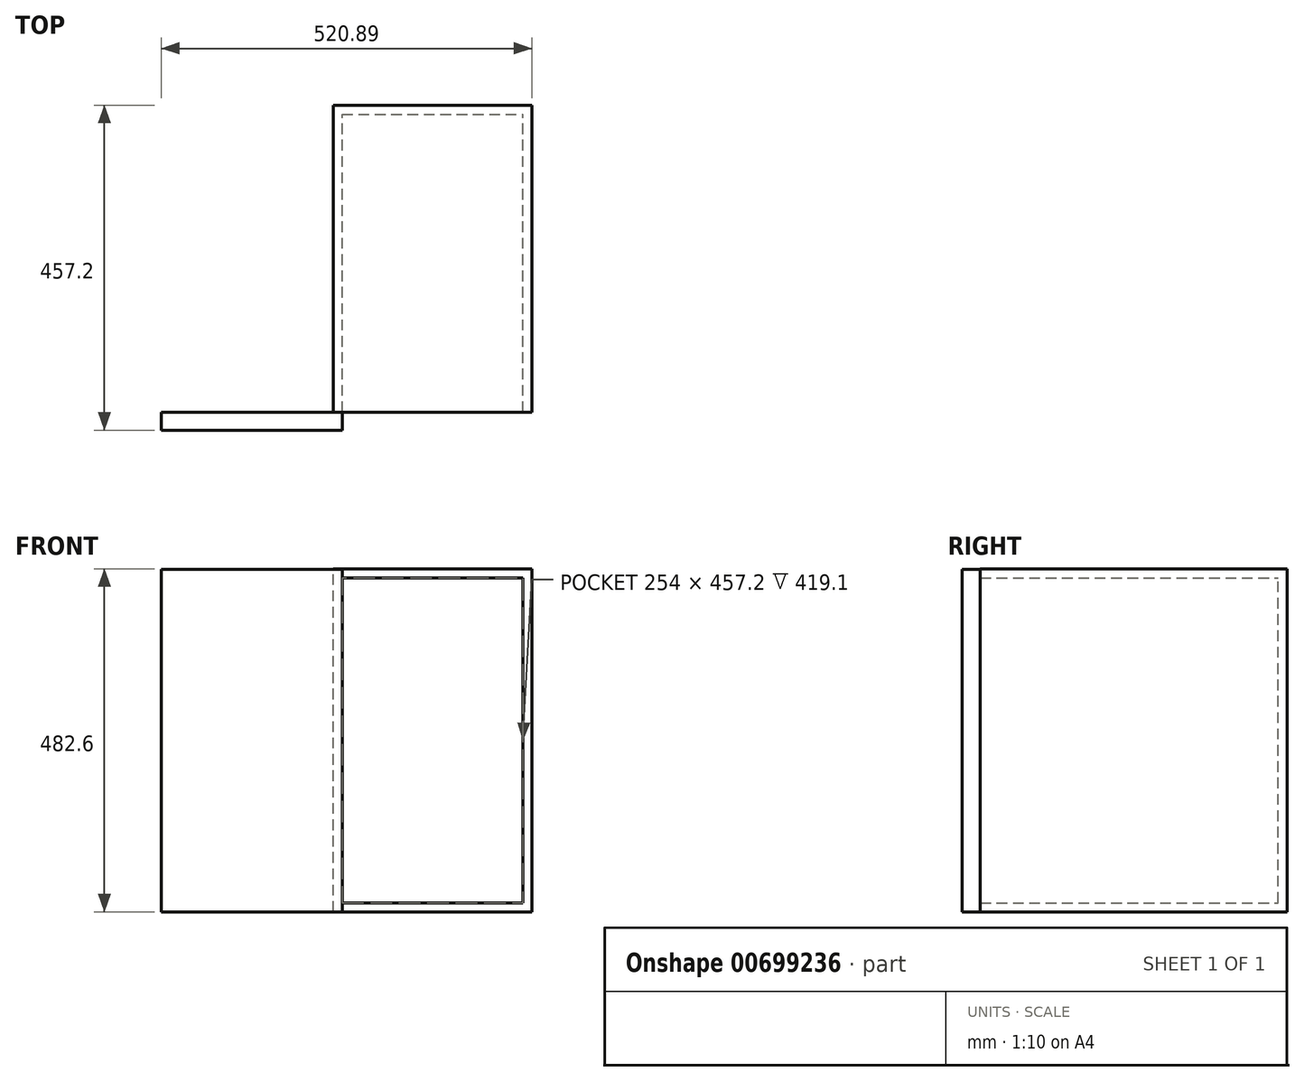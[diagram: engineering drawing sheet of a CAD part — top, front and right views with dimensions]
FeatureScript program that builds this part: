
annotation { "Feature Type Name" : "Feature", "Feature Type Description" : "" }
export const myFeature = defineFeature(function(context is Context, id is Id, definition is map)
    precondition{}
    {
        {
            var Q0;
            Q0=qCreatedBy(makeId("Front.planeOp"),FACE);
            var sketch = newSketch(context, id + "F0", { "sketchPlane" : qUnion([Q0])});
            skLineSegment(sketch, "E0.bottom", {"start": v(-18.31, -76.13) * mm, "end": v(261.09, -76.13) * mm});
            skLineSegment(sketch, "E0.top", {"start": v(-18.31, 406.47) * mm, "end": v(261.09, 406.47) * mm});
            skLineSegment(sketch, "E0.left", {"start": v(-18.31, -76.13) * mm, "end": v(-18.31, 406.47) * mm});
            skLineSegment(sketch, "E0.right", {"start": v(261.09, -76.13) * mm, "end": v(261.09, 406.47) * mm});
            skSolve(sketch);
        }
        {
            var Q0;
            Q0=makeQuery(id+"F0.imprint","IMPRINT",FACE,{"disambiguationData":[TD([[makeQuery(id+"F0.imprint","IMPRINT",EDGE,{"derivedFrom":sQuery(id+"F0.wireOp",EDGE,"E0.bottom")}),1.0]])]});
            extrude(context, id + "F1", {"entities" : qUnion([Q0]), "depth" : 431.8 * mm, "offsetDistance" : 25.4 * mm});
        }
        {
            var Q0;
            Q0=makeQuery(id+"F1.opExtrude","CAP_FACE",FACE,{"disambiguationData":[OSD([sQuery(id+"F0.wireOp",EDGE,"E0.bottom"),sQuery(id+"F0.wireOp",EDGE,"E0.top"),sQuery(id+"F0.wireOp",EDGE,"E0.left"),sQuery(id+"F0.wireOp",EDGE,"E0.right")])],"isStart":false});
            shell(context, id + "F2", {"entities" : qUnion([Q0]), "thickness" : 12.7 * mm});
        }
        {
            var Q0;
            Q0=makeQuery(id+"F1.opExtrude","CAP_FACE",FACE,{"disambiguationData":[OSD([sQuery(id+"F0.wireOp",EDGE,"E0.bottom"),sQuery(id+"F0.wireOp",EDGE,"E0.top"),sQuery(id+"F0.wireOp",EDGE,"E0.left"),sQuery(id+"F0.wireOp",EDGE,"E0.right")])],"isStart":false});
            var sketch = newSketch(context, id + "F3", { "sketchPlane" : qUnion([Q0])});
            skLineSegment(sketch, "E1.bottom", {"start": v(-5.61, -76.13) * mm, "end": v(-259.8, -76.13) * mm});
            skLineSegment(sketch, "E1.top", {"start": v(-5.61, 405.65) * mm, "end": v(-259.8, 405.65) * mm});
            skLineSegment(sketch, "E1.left", {"start": v(-5.61, -76.13) * mm, "end": v(-5.61, 405.65) * mm});
            skLineSegment(sketch, "E1.right", {"start": v(-259.8, -76.13) * mm, "end": v(-259.8, 405.65) * mm});
            skSolve(sketch);
        }
        {
            var Q0;
            Q0 = qSketchRegion(id + "F3", true);
            extrude(context, id + "F4", {"entities" : qUnion([Q0]), "operationType" : NewBodyOperationType.ADD, "depth" : 25.4 * mm, "offsetDistance" : 25.4 * mm});
        }
    });
